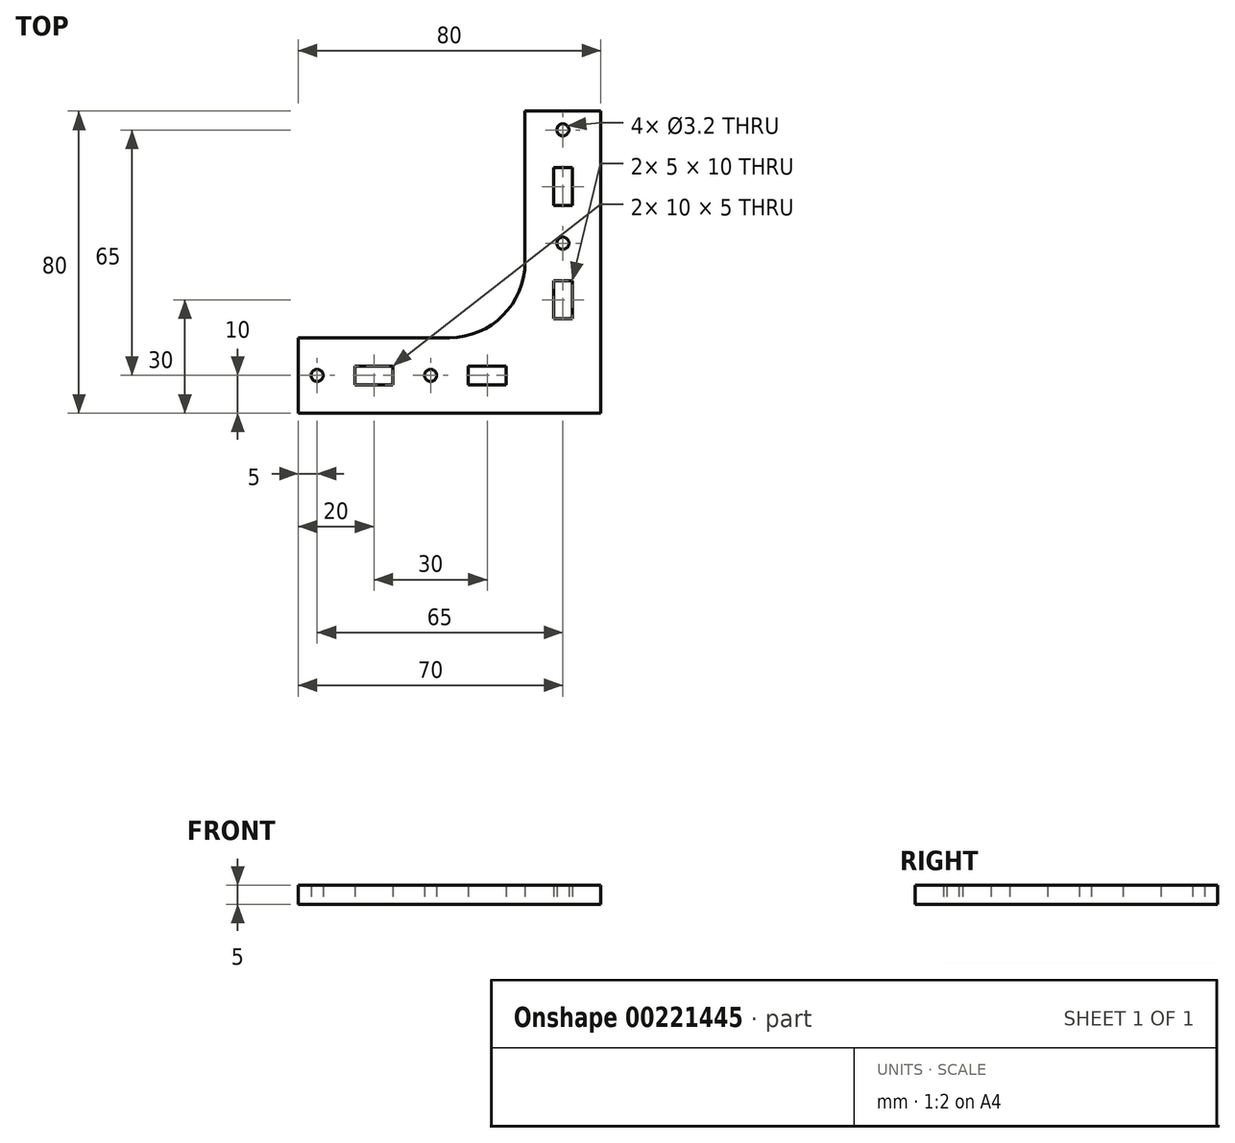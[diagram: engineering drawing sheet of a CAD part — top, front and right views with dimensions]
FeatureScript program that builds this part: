
annotation { "Feature Type Name" : "Feature", "Feature Type Description" : "" }
export const myFeature = defineFeature(function(context is Context, id is Id, definition is map)
    precondition{}
    {
        {
            assignVariable(context, id + "F0", {"name" : "thickness", "anyValue" : 5 * mm});
        }
        {
            var Q0;
            Q0=qCreatedBy(makeId("Top.planeOp"),FACE);
            var sketch = newSketch(context, id + "F1", { "sketchPlane" : qUnion([Q0])});
            skLineSegment(sketch, "E0", {"start": v(0, 0) * mm, "end": v(-80, 0) * mm});
            skLineSegment(sketch, "E1", {"start": v(-70, 0) * mm, "end": v(-70, 20) * mm, "construction": true});
            skLineSegment(sketch, "E2", {"start": v(-80, 20) * mm, "end": v(-40, 20) * mm});
            skLineSegment(sketch, "E3", {"start": v(-20, 40) * mm, "end": v(-20, 80) * mm});
            skLineSegment(sketch, "E4", {"start": v(-20, 70) * mm, "end": v(0, 70) * mm, "construction": true});
            skLineSegment(sketch, "E5", {"start": v(0, 80) * mm, "end": v(0, 0) * mm});
            skLineSegment(sketch, "E6", {"start": v(-70, 10) * mm, "end": v(-10, 10) * mm, "construction": true});
            skLineSegment(sketch, "E7", {"start": v(-10, 70) * mm, "end": v(-10, 10) * mm, "construction": true});
            skLineSegment(sketch, "E8.bottom", {"start": v(-55, 12.5) * mm, "end": v(-65, 12.5) * mm});
            skLineSegment(sketch, "E8.top", {"start": v(-55, 7.5) * mm, "end": v(-65, 7.5) * mm});
            skLineSegment(sketch, "E8.left", {"start": v(-55, 12.5) * mm, "end": v(-55, 7.5) * mm});
            skLineSegment(sketch, "E8.right", {"start": v(-65, 12.5) * mm, "end": v(-65, 7.5) * mm});
            skPoint(sketch, "E8.middle", {"position": v(-60, 10) * mm});
            skLineSegment(sketch, "E9.bottom", {"start": v(-25, 12.5) * mm, "end": v(-35, 12.5) * mm});
            skLineSegment(sketch, "E9.top", {"start": v(-25, 7.5) * mm, "end": v(-35, 7.5) * mm});
            skLineSegment(sketch, "E9.left", {"start": v(-25, 12.5) * mm, "end": v(-25, 7.5) * mm});
            skLineSegment(sketch, "E9.right", {"start": v(-35, 12.5) * mm, "end": v(-35, 7.5) * mm});
            skPoint(sketch, "E9.middle", {"position": v(-30, 10) * mm});
            skLineSegment(sketch, "E10.bottom", {"start": v(-7.5, 35) * mm, "end": v(-12.5, 35) * mm});
            skLineSegment(sketch, "E10.top", {"start": v(-7.5, 25) * mm, "end": v(-12.5, 25) * mm});
            skLineSegment(sketch, "E10.left", {"start": v(-7.5, 35) * mm, "end": v(-7.5, 25) * mm});
            skLineSegment(sketch, "E10.right", {"start": v(-12.5, 35) * mm, "end": v(-12.5, 25) * mm});
            skPoint(sketch, "E10.middle", {"position": v(-10, 30) * mm});
            skLineSegment(sketch, "E11.bottom", {"start": v(-7.5, 65) * mm, "end": v(-12.5, 65) * mm});
            skLineSegment(sketch, "E11.top", {"start": v(-7.5, 55) * mm, "end": v(-12.5, 55) * mm});
            skLineSegment(sketch, "E11.left", {"start": v(-7.5, 65) * mm, "end": v(-7.5, 55) * mm});
            skLineSegment(sketch, "E11.right", {"start": v(-12.5, 65) * mm, "end": v(-12.5, 55) * mm});
            skPoint(sketch, "E11.middle", {"position": v(-10, 60) * mm});
            skCircle(sketch, "E12", {"center": v(-45, 10) * mm, "radius": 1.6 * mm});
            skCircle(sketch, "E13", {"center": v(-10, 45) * mm, "radius": 1.6 * mm});
            skPoint(sketch, "E14.visualSharp", {"position": v(-20, 20) * mm});
            skArc(sketch, "E14.filletArc", {"start": v(-40, 20) * mm, "mid": v(-25.86, 25.86) * mm, "end": v(-20, 40) * mm});
            skPoint(sketch, "E15.visualSharp", {"position": v(-70, 20) * mm});
            skPoint(sketch, "E16.visualSharp", {"position": v(-70, 0) * mm});
            skPoint(sketch, "E17.visualSharp", {"position": v(-20, 70) * mm});
            skPoint(sketch, "E18.visualSharp", {"position": v(0, 70) * mm});
            skLineSegment(sketch, "E19", {"start": v(-80, 20) * mm, "end": v(-80, 0) * mm});
            skCircle(sketch, "E20", {"center": v(-75, 10) * mm, "radius": 1.6 * mm});
            skPoint(sketch, "E20.centerSnap0", {"position": v(-80, 10) * mm});
            skLineSegment(sketch, "E21", {"start": v(0, 80) * mm, "end": v(-20, 80) * mm});
            skCircle(sketch, "E22", {"center": v(-10, 75) * mm, "radius": 1.6 * mm});
            skPoint(sketch, "E22.centerSnap0", {"position": v(-10, 80) * mm});
            skSolve(sketch);
        }
        {
            var Q0;
            Q0 = qSketchRegion(id + "F1", true);
            extrude(context, id + "F2", {"entities" : qUnion([Q0]), "depth" : getVariable(context, 'thickness')});
        }
    });
